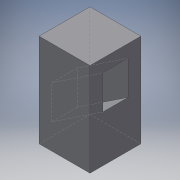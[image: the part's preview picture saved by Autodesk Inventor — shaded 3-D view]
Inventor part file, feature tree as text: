
AUTODESK INVENTOR PART (.ipt)
format: ipt  version: 2016 (Build 200138000, 138)  size: 108,544 bytes
history: native  units: in
note: dims shown in document units (in); Inventor stores cm internally (conversion verified against a paired STEP export)
features: extrude x3, sketch x3
ambient origin geometry x8: Origin, YZ Plane, XZ Plane, XY Plane, X Axis, Y Axis, Z Axis, Center Point
bodies: Solid1 (feature_tree)
feature tree (6):
  extrude  "Extrusion1"  Depth=3.0in
  extrude  "Extrusion2"  Depth=3.0in
  extrude  "Extrusion3"  Depth=1.5in TaperAngle=0.0deg
  sketch  "Sketch1"  dims[d0=5.5in d1=3.0in]
  sketch  "Sketch2"  dims[d2=3.0in d3=0.5in]
  sketch  "Sketch3"  dims[d5=0.5in d6=1.5in d7=0.0in d8=0.75in d9=0.0in d10=0.75in d11=0.0in d12=3.0in]
